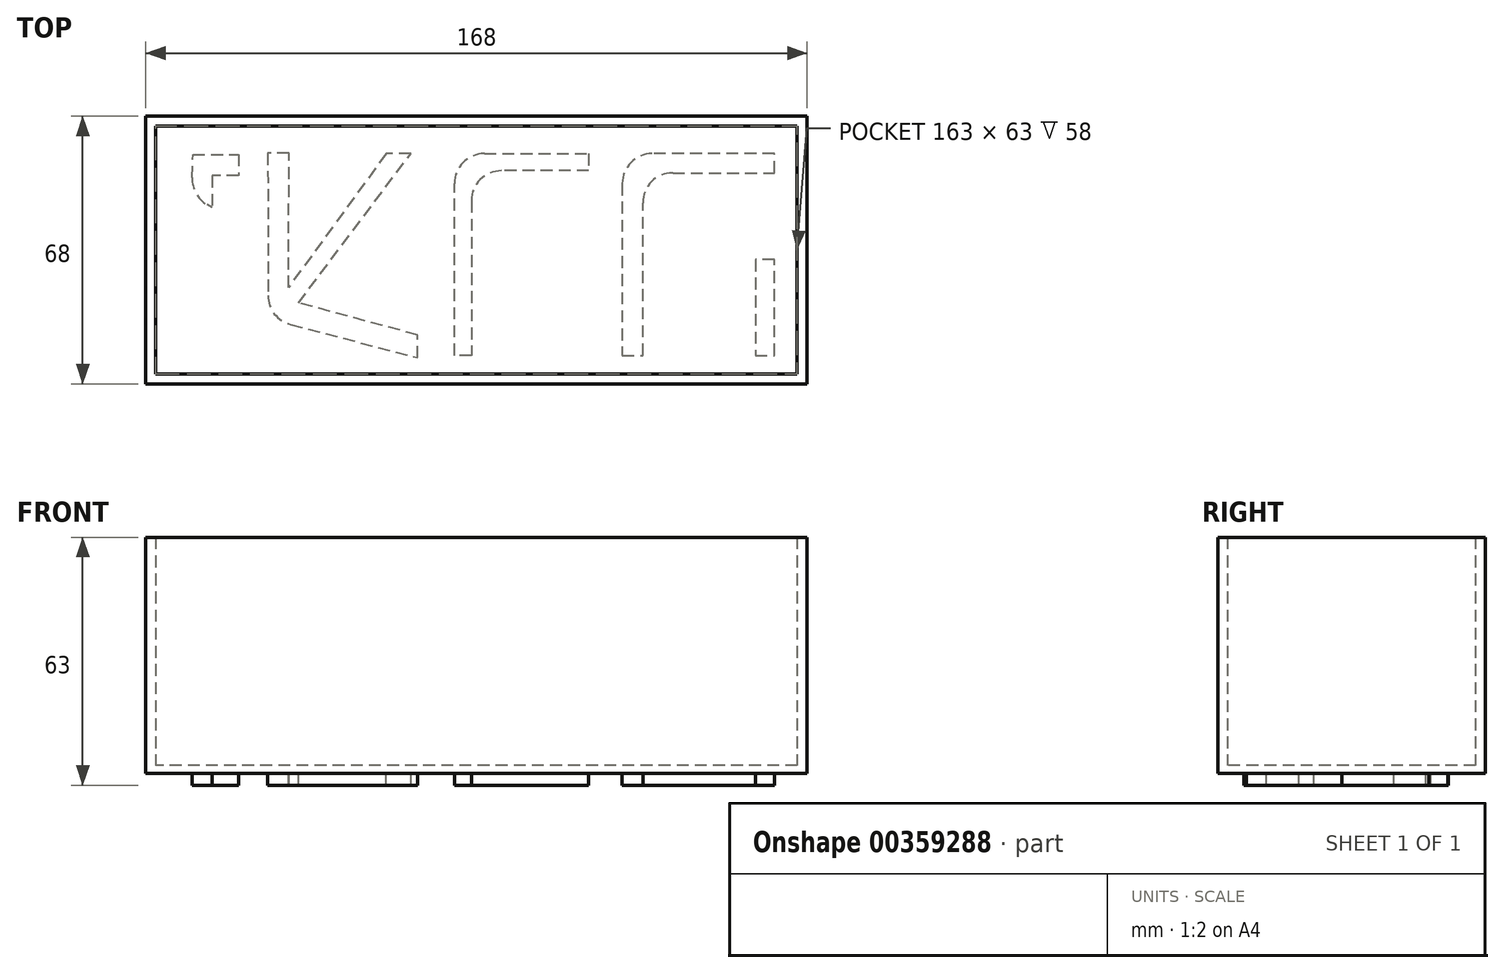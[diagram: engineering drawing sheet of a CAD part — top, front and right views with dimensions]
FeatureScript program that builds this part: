
annotation { "Feature Type Name" : "Feature", "Feature Type Description" : "" }
export const myFeature = defineFeature(function(context is Context, id is Id, definition is map)
    precondition{}
    {
        {
            var Q0;
            Q0=qCreatedBy(makeId("Top.planeOp"),FACE);
            var sketch = newSketch(context, id + "F0", { "sketchPlane" : qUnion([Q0])});
            skLineSegment(sketch, "E0.bottom", {"start": v(81.5, 31.5) * mm, "end": v(-81.5, 31.5) * mm});
            skLineSegment(sketch, "E0.top", {"start": v(81.5, -31.5) * mm, "end": v(-81.5, -31.5) * mm});
            skLineSegment(sketch, "E0.left", {"start": v(81.5, 31.5) * mm, "end": v(81.5, -31.5) * mm});
            skLineSegment(sketch, "E0.right", {"start": v(-81.5, 31.5) * mm, "end": v(-81.5, -31.5) * mm});
            skPoint(sketch, "E0.middle", {"position": v(0, 0) * mm});
            skLineSegment(sketch, "E1.bottom", {"start": v(84, 34) * mm, "end": v(-84, 34) * mm});
            skLineSegment(sketch, "E1.top", {"start": v(84, -34) * mm, "end": v(-84, -34) * mm});
            skLineSegment(sketch, "E1.left", {"start": v(84, 34) * mm, "end": v(84, -34) * mm});
            skLineSegment(sketch, "E1.right", {"start": v(-84, 34) * mm, "end": v(-84, -34) * mm});
            skSolve(sketch);
        }
        {
            var Q0;
            Q0=makeQuery(id+"F0.imprint","IMPRINT",FACE,{"disambiguationData":[TD([[makeQuery(id+"F0.imprint","IMPRINT",EDGE,{"derivedFrom":sQuery(id+"F0.wireOp",EDGE,"E0.bottom")}),-1.0]])]});
            extrude(context, id + "F1", {"entities" : qUnion([Q0]), "depth" : 60 * mm});
        }
        {
            var Q0;
            Q0=makeQuery(id+"F0.imprint","IMPRINT",FACE,{"disambiguationData":[TD([[makeQuery(id+"F0.imprint","IMPRINT",EDGE,{"derivedFrom":sQuery(id+"F0.wireOp",EDGE,"E0.bottom")}),1.0]])]});
            extrude(context, id + "F2", {"entities" : qUnion([Q0]), "operationType" : NewBodyOperationType.ADD, "depth" : 2 * mm});
        }
        {
            var Q0;
            Q0=makeQuery(id+"F0.imprint","IMPRINT",FACE,{"disambiguationData":[TD([[makeQuery(id+"F0.imprint","IMPRINT",EDGE,{"derivedFrom":sQuery(id+"F0.wireOp",EDGE,"E0.bottom")}),1.0]])]});
            var sketch = newSketch(context, id + "F3", { "sketchPlane" : qUnion([Q0])});
            skLineSegment(sketch, "E2", {"start": v(-72, 24.3) * mm, "end": v(-60.44, 24.3) * mm});
            skLineSegment(sketch, "E3", {"start": v(-60.44, 24.3) * mm, "end": v(-60.44, 18.88) * mm});
            skLineSegment(sketch, "E4", {"start": v(-60.44, 18.88) * mm, "end": v(-67.13, 18.88) * mm});
            skLineSegment(sketch, "E5", {"start": v(-67.13, 18.88) * mm, "end": v(-67.13, 10.75) * mm});
            skLineSegment(sketch, "E6", {"start": v(-67.13, 10.75) * mm, "end": v(-68.45, 11.53) * mm});
            skLineSegment(sketch, "E7", {"start": v(-72.2, 18.36) * mm, "end": v(-72, 24.3) * mm});
            skLineSegment(sketch, "E8", {"start": v(-53, 24.63) * mm, "end": v(-52.93, -11.57) * mm});
            skLineSegment(sketch, "E9", {"start": v(-47.24, -18.92) * mm, "end": v(-15, -27.37) * mm});
            skLineSegment(sketch, "E10", {"start": v(-15, -27.37) * mm, "end": v(-15, -21.59) * mm});
            skLineSegment(sketch, "E11", {"start": v(-15, -21.59) * mm, "end": v(-45.22, -13.4) * mm});
            skLineSegment(sketch, "E12", {"start": v(-45.22, -13.4) * mm, "end": v(-16.65, 24.48) * mm});
            skLineSegment(sketch, "E13", {"start": v(-16.65, 24.48) * mm, "end": v(-22.94, 24.48) * mm});
            skLineSegment(sketch, "E14", {"start": v(-22.94, 24.48) * mm, "end": v(-47.74, -9.53) * mm});
            skLineSegment(sketch, "E15", {"start": v(-47.74, -9.53) * mm, "end": v(-47.6, 24.63) * mm});
            skLineSegment(sketch, "E16", {"start": v(-47.6, 24.63) * mm, "end": v(-53, 24.63) * mm});
            skLineSegment(sketch, "E17", {"start": v(-5.6, -26.76) * mm, "end": v(-5.6, 16.86) * mm});
            skLineSegment(sketch, "E18", {"start": v(2.02, 24.48) * mm, "end": v(28.54, 24.48) * mm});
            skLineSegment(sketch, "E19", {"start": v(28.54, 24.48) * mm, "end": v(28.54, 20.14) * mm});
            skLineSegment(sketch, "E20", {"start": v(28.54, 20.14) * mm, "end": v(6.36, 20.14) * mm});
            skLineSegment(sketch, "E21", {"start": v(-1.26, 12.52) * mm, "end": v(-1.26, -26.76) * mm});
            skLineSegment(sketch, "E22", {"start": v(-1.26, -26.76) * mm, "end": v(-5.6, -26.76) * mm});
            skLineSegment(sketch, "E23", {"start": v(37.03, 16.86) * mm, "end": v(37.03, -26.76) * mm});
            skLineSegment(sketch, "E24", {"start": v(37.03, -26.76) * mm, "end": v(42.27, -26.76) * mm});
            skLineSegment(sketch, "E25", {"start": v(42.27, -26.76) * mm, "end": v(42.27, 11.98) * mm});
            skLineSegment(sketch, "E26", {"start": v(49.9, 19.6) * mm, "end": v(75.7, 19.6) * mm});
            skLineSegment(sketch, "E27", {"start": v(75.7, 19.6) * mm, "end": v(75.7, 24.48) * mm});
            skLineSegment(sketch, "E28", {"start": v(75.7, 24.48) * mm, "end": v(44.65, 24.48) * mm});
            skLineSegment(sketch, "E29", {"start": v(70.87, -2.4) * mm, "end": v(70.87, -26.76) * mm});
            skLineSegment(sketch, "E30", {"start": v(70.87, -26.76) * mm, "end": v(75.7, -26.76) * mm});
            skLineSegment(sketch, "E31", {"start": v(75.7, -26.76) * mm, "end": v(75.7, -2.4) * mm});
            skLineSegment(sketch, "E32", {"start": v(75.7, -2.4) * mm, "end": v(70.87, -2.4) * mm});
            skPoint(sketch, "E33.visualSharp", {"position": v(-72.37, 13.82) * mm});
            skArc(sketch, "E33.filletArc", {"start": v(-72.2, 18.36) * mm, "mid": v(-71.27, 14.43) * mm, "end": v(-68.45, 11.53) * mm});
            skPoint(sketch, "E34.visualSharp", {"position": v(42.27, 19.6) * mm});
            skArc(sketch, "E34.filletArc", {"start": v(49.9, 19.6) * mm, "mid": v(44.5, 17.37) * mm, "end": v(42.27, 11.98) * mm});
            skPoint(sketch, "E35.visualSharp", {"position": v(37.03, 24.48) * mm});
            skArc(sketch, "E35.filletArc", {"start": v(44.65, 24.48) * mm, "mid": v(39.27, 22.25) * mm, "end": v(37.03, 16.86) * mm});
            skPoint(sketch, "E36.visualSharp", {"position": v(-5.6, 24.48) * mm});
            skArc(sketch, "E36.filletArc", {"start": v(2.02, 24.48) * mm, "mid": v(-3.37, 22.25) * mm, "end": v(-5.6, 16.86) * mm});
            skPoint(sketch, "E37.visualSharp", {"position": v(-1.26, 20.14) * mm});
            skArc(sketch, "E37.filletArc", {"start": v(6.36, 20.14) * mm, "mid": v(0.97, 17.91) * mm, "end": v(-1.26, 12.52) * mm});
            skPoint(sketch, "E38.visualSharp", {"position": v(-52.92, -17.44) * mm});
            skArc(sketch, "E38.filletArc", {"start": v(-52.93, -11.57) * mm, "mid": v(-51.34, -16.21) * mm, "end": v(-47.24, -18.92) * mm});
            skPoint(sketch, "E39.endSnap0", {"position": v(-3.37, 22.25) * mm});
            skSolve(sketch);
        }
        {
            var Q0;
            Q0 = qSketchRegion(id + "F3", true);
            extrude(context, id + "F4", {"entities" : qUnion([Q0]), "operationType" : NewBodyOperationType.ADD, "oppositeDirection" : true, "depth" : 3 * mm});
        }
    });
